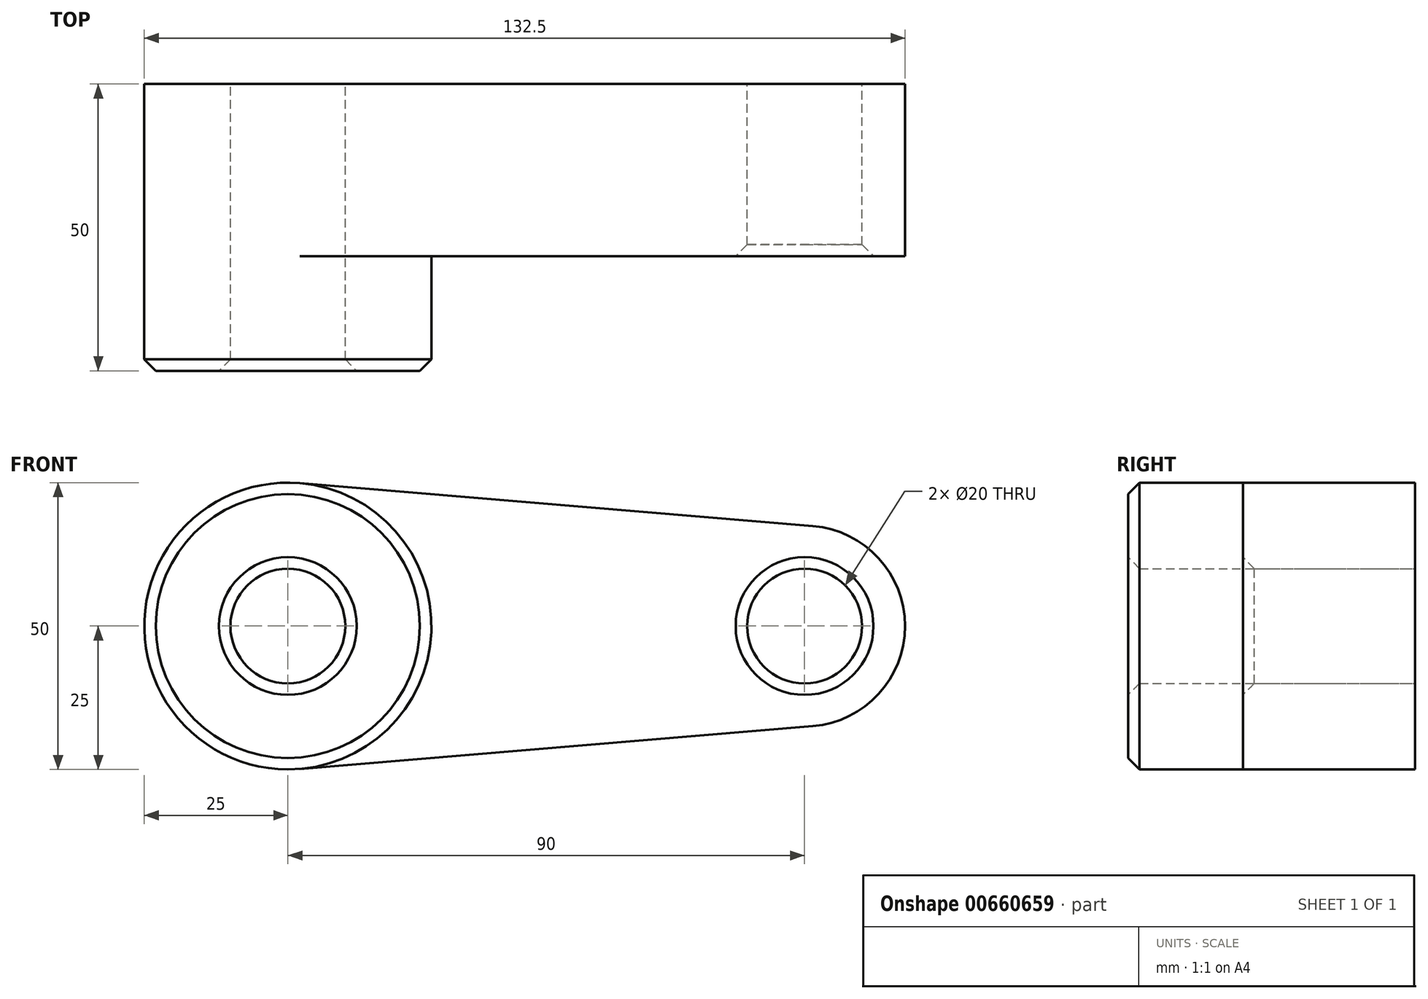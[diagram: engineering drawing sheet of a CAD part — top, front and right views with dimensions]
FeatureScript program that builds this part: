
annotation { "Feature Type Name" : "Feature", "Feature Type Description" : "" }
export const myFeature = defineFeature(function(context is Context, id is Id, definition is map)
    precondition{}
    {
        {
            var Q0;
            Q0=qCreatedBy(makeId("Front.planeOp"),FACE);
            var sketch = newSketch(context, id + "F0", { "sketchPlane" : qUnion([Q0])});
            skCircle(sketch, "E0", {"center": v(0, 0) * mm, "radius": 25 * mm});
            skCircle(sketch, "E1", {"center": v(90, 0) * mm, "radius": 17.5 * mm});
            skLineSegment(sketch, "E2", {"start": v(2.08, 24.91) * mm, "end": v(91.46, 17.44) * mm});
            skLineSegment(sketch, "E3", {"start": v(2.08, -24.91) * mm, "end": v(91.46, -17.44) * mm});
            skCircle(sketch, "E4", {"center": v(0, 0) * mm, "radius": 10 * mm});
            skCircle(sketch, "E5", {"center": v(90, 0) * mm, "radius": 10 * mm});
            skSolve(sketch);
        }
        {
            var Q0;
            Q0=qSketchRegion(id+"F0",true);
            extrude(context, id + "F1", {"entities" : qUnion([Q0]), "depth" : 30 * mm, "offsetDistance" : 25 * mm});
        }
        {
            var Q0;
            Q0=makeQuery(id+"F0.imprint","IMPRINT",FACE,{"disambiguationData":[TD([[makeQuery(id+"F0.imprint","IMPRINT",EDGE,{"derivedFrom":sQuery(id+"F0.wireOp",EDGE,"E4")}),-1.0]])]});
            extrude(context, id + "F2", {"entities" : qUnion([Q0]), "operationType" : NewBodyOperationType.ADD, "depth" : 50 * mm});
        }
        {
            var Q0;
            Q0=makeQuery(id+"F2.opExtrude","CAP_EDGE",EDGE,{"disambiguationData":[OSD([sQuery(id+"F0.wireOp",EDGE,"E0")])],"isStart":false});
            var Q1;
            Q1=makeQuery(id+"F2.opExtrude","CAP_EDGE",EDGE,{"disambiguationData":[OSD([sQuery(id+"F0.wireOp",EDGE,"E4")])],"isStart":false});
            var Q2;
            Q2=makeQuery(id+"F1.opExtrude","CAP_EDGE",EDGE,{"disambiguationData":[OSD([sQuery(id+"F0.wireOp",EDGE,"E5")])],"isStart":false});
            chamfer(context, id + "F3", {"entities" : qUnion([Q0, Q1, Q2]), "width" : 2 * mm, "tangentPropagation" : true});
        }
    });
